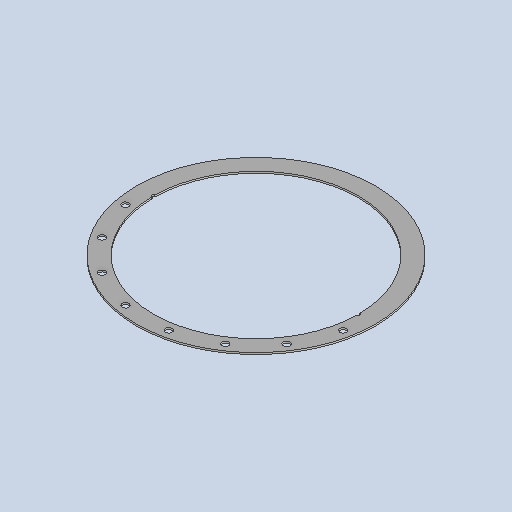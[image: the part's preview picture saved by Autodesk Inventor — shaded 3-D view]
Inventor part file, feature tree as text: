
AUTODESK INVENTOR PART (.ipt)
format: ipt  version: 2025 (Build 290162010, 162A)  size: 163,328 bytes
history: native  units: mm
features: sketch x3, extrude x2, other x2, sheet_metal_op x1, pattern_circular x1, projected_geometry x1
ambient origin geometry x8: Origin, YZ Plane, XZ Plane, XY Plane, X Axis, Y Axis, Z Axis, Center Point
bodies: Solid1 (feature_tree)
feature tree (10):
  sheet_metal_op  "Face1"
  extrude  "Extrusion1"  TaperAngle=0.0deg  [1 undecoded]
  pattern_circular  "Circular Pattern1"  Count=8 Angle=157.5deg
  extrude  "Extrusion2"  Depth=30.0mm
  sketch  "Sketch1"  dims[d2=3.0mm d4=0.0mm d5=0.0mm d6=80.0mm d7=157.5deg]
  other  "Plate1"
  sketch  "Sketch2"  dims[d9=390.0mm d11=30.0mm]
  projected_geometry  "Projected Loop1"
  sketch  "Sketch3"  dims[d20=1.963495mm d21=12.0mm d25=0.0mm d26=0.0mm d27=5.0mm d29=80.0mm d30=0.5mm d31=0.872665mm d32=0.5mm d33=0.872665mm]
  other  "Definition1"
note: 1 required parameter value undecoded (feature->parameter linkage not recoverable at this tier; creation-order binding heuristic only, values carry confidence <= 0.55)
